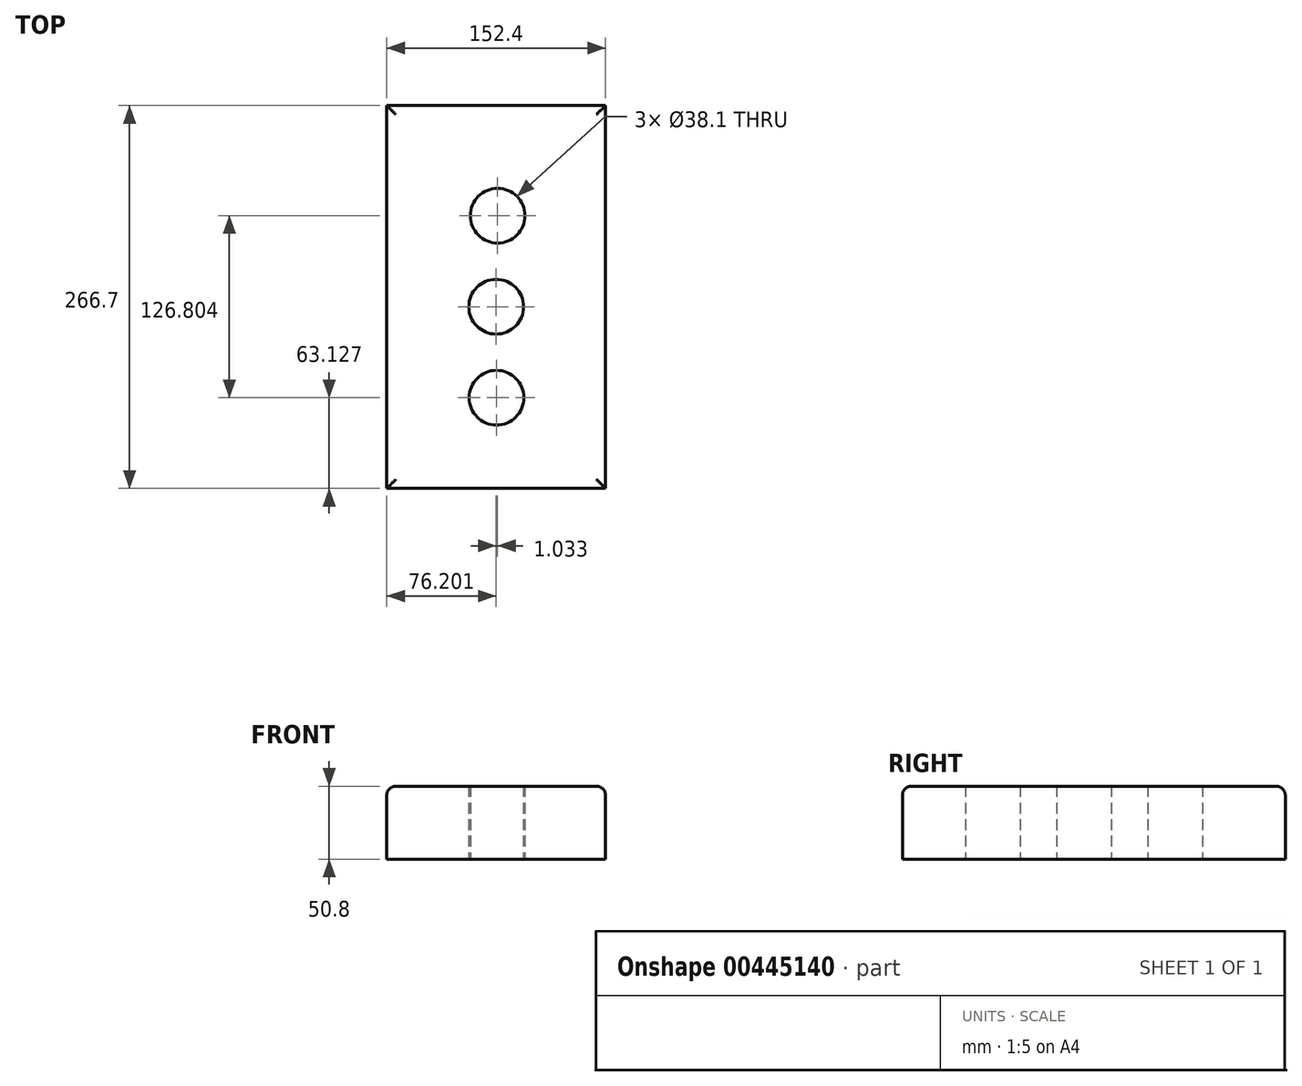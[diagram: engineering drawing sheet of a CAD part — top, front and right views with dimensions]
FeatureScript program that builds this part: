
annotation { "Feature Type Name" : "Feature", "Feature Type Description" : "" }
export const myFeature = defineFeature(function(context is Context, id is Id, definition is map)
    precondition{}
    {
        {
            var Q0;
            Q0=qCreatedBy(makeId("Top.planeOp"),FACE);
            var sketch = newSketch(context, id + "F0", { "sketchPlane" : qUnion([Q0])});
            skLineSegment(sketch, "E0.bottom", {"start": v(-72.25, 177.23) * mm, "end": v(80.15, 177.23) * mm});
            skLineSegment(sketch, "E0.top", {"start": v(-72.25, -89.47) * mm, "end": v(80.15, -89.47) * mm});
            skLineSegment(sketch, "E0.left", {"start": v(-72.25, 177.23) * mm, "end": v(-72.25, -89.47) * mm});
            skLineSegment(sketch, "E0.right", {"start": v(80.15, 177.23) * mm, "end": v(80.15, -89.47) * mm});
            skPoint(sketch, "E1.centerSnap0", {"position": v(3.95, 177.23) * mm});
            skCircle(sketch, "E2", {"center": v(3.95, 37.02) * mm, "radius": 19.05 * mm});
            skLineSegment(sketch, "E3", {"start": v(2.48, 18.03) * mm, "end": v(2.48, -7.37) * mm});
            skCircle(sketch, "E4", {"center": v(4.2, -26.34) * mm, "radius": 19.05 * mm});
            skPoint(sketch, "E4.second.point", {"position": v(2.48, -45.32) * mm});
            skPoint(sketch, "E4.third.point", {"position": v(22.74, -30.68) * mm});
            skLineSegment(sketch, "E5", {"start": v(3.52, 56.07) * mm, "end": v(3.52, 81.47) * mm});
            skCircle(sketch, "E6", {"center": v(4.98, 100.46) * mm, "radius": 19.05 * mm});
            skPoint(sketch, "E6.second.point", {"position": v(3.52, 119.45) * mm});
            skPoint(sketch, "E6.third.point", {"position": v(23.92, 102.55) * mm});
            skSolve(sketch);
        }
        {
            var Q0;
            Q0 = qSketchRegion(id + "F0", true);
            extrude(context, id + "F1", {"entities" : qUnion([Q0]), "depth" : 50.8 * mm});
        }
        {
            var Q0;
            Q0=makeQuery(id+"F1.opExtrude","CAP_EDGE",EDGE,{"disambiguationData":[OSD([sQuery(id+"F0.wireOp",EDGE,"E0.top")])],"isStart":false});
            var Q1;
            Q1=makeQuery(id+"F1.opExtrude","CAP_EDGE",EDGE,{"disambiguationData":[OSD([sQuery(id+"F0.wireOp",EDGE,"E0.right")])],"isStart":false});
            var Q2;
            Q2=makeQuery(id+"F1.opExtrude","CAP_EDGE",EDGE,{"disambiguationData":[OSD([sQuery(id+"F0.wireOp",EDGE,"E0.bottom")])],"isStart":false});
            var Q3;
            Q3=makeQuery(id+"F1.opExtrude","CAP_EDGE",EDGE,{"disambiguationData":[OSD([sQuery(id+"F0.wireOp",EDGE,"E0.left")])],"isStart":false});
            fillet(context, id + "F2", {"entities" : qUnion([Q0, Q1, Q2, Q3]), "radius" : 6.35 * mm, "tangentPropagation" : true, "allowEdgeOverflow" : false});
        }
    });
